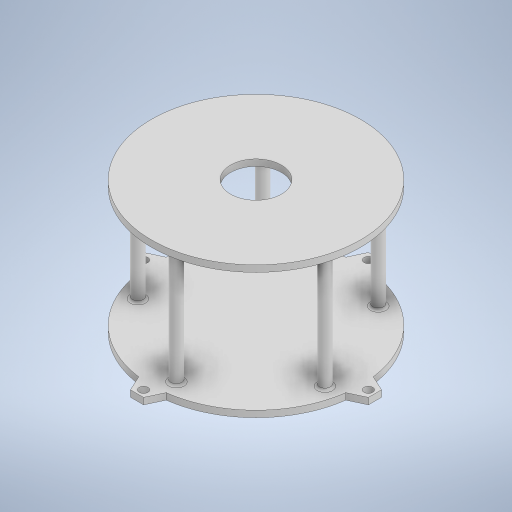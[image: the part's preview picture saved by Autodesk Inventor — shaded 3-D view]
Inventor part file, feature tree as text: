
AUTODESK INVENTOR PART (.ipt)
format: ipt  version: 2023 (Build 270158000, 158)  size: 329,216 bytes
history: native  units: mm
features: extrude x5, sketch x5, pattern_circular x2, other x1, plane x1, fillet x1
ambient origin geometry x8: Origin, YZ Plane, XZ Plane, XY Plane, X Axis, Y Axis, Z Axis, Center Point
bodies: Body1 (feature_tree)
feature tree (15):
  other  "Sólido1"
  extrude  "Extrusión1"  Depth=2.96mm TaperAngle=0.0deg
  plane  "Plano de trabajo1"
  extrude  "Extrusión2"  Depth=2.96mm TaperAngle=0.0deg
  extrude  "Extrusión3"  Depth=4.0mm
  pattern_circular  "Patrón circular1"  [2 undecoded]
  extrude  "Extrusión4"  Depth=10.0mm
  fillet  "Empalme1"  Radius=2.96mm
  pattern_circular  "Patrón circular2"  Count=4 Angle=360.0deg
  extrude  "Extrusión5"  Depth=10.0mm
  sketch  "Boceto1"  dims[d0=95.7mm d1=2.96mm d2=0.0mm]
  sketch  "Boceto2"  dims[d3=54.7mm d4=2.96mm d5=0.0mm]
  sketch  "Boceto3"  dims[d6=103.0mm d7=4.0mm]
  sketch  "Boceto4"  dims[d8=20.071286mm]
  sketch  "Boceto5"  dims[d9=20.071286mm d10=3.0mm d11=6.0mm d12=2.96mm d13=0.0mm d14=40.0mm d15=360.0deg d17=82.0mm d18=30.0deg d19=5.0mm d20=2.96mm d21=0.0mm d22=1.0mm d23=50.0mm d24=360.0deg d26=23.2mm d27=10.0mm d28=0.0mm d25=0.0mm]
note: 2 required parameter values undecoded (feature->parameter linkage not recoverable at this tier; creation-order binding heuristic only, values carry confidence <= 0.55)
